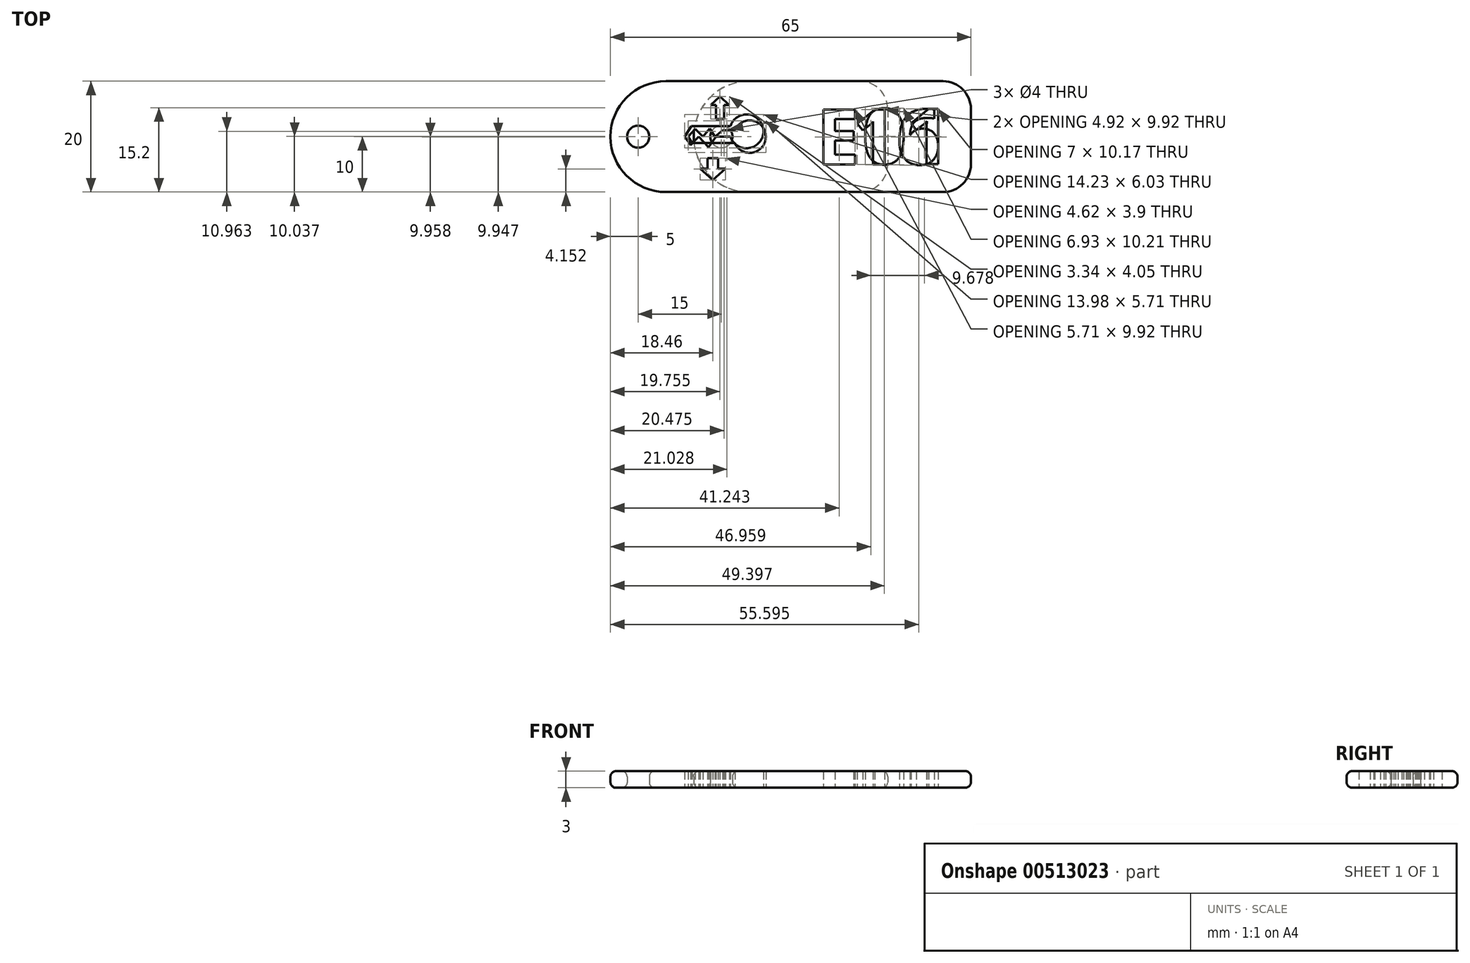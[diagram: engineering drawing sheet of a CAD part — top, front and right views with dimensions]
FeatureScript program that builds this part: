
annotation { "Feature Type Name" : "Feature", "Feature Type Description" : "" }
export const myFeature = defineFeature(function(context is Context, id is Id, definition is map)
    precondition{}
    {
        {
            var Q0;
            Q0=qCreatedBy(makeId("Top.planeOp"),FACE);
            var sketch = newSketch(context, id + "F0", { "sketchPlane" : qUnion([Q0])});
            skLineSegment(sketch, "E0.bottom", {"start": v(27.5, 10) * mm, "end": v(-22.5, 10) * mm});
            skLineSegment(sketch, "E0.top", {"start": v(27.5, -10) * mm, "end": v(-22.5, -10) * mm});
            skLineSegment(sketch, "E0.left", {"start": v(32.5, 5) * mm, "end": v(32.5, -5) * mm});
            skLineSegment(sketch, "E0.right", {"start": v(-32.5, 0) * mm, "end": v(-32.5, 0) * mm});
            skPoint(sketch, "E0.middle", {"position": v(0, 0) * mm});
            skPoint(sketch, "E1.visualSharp", {"position": v(-32.5, 10) * mm});
            skArc(sketch, "E1.filletArc", {"start": v(-22.5, 10) * mm, "mid": v(-29.57, 7.07) * mm, "end": v(-32.5, 0) * mm});
            skPoint(sketch, "E2.visualSharp", {"position": v(-32.5, -10) * mm});
            skArc(sketch, "E2.filletArc", {"start": v(-32.5, 0) * mm, "mid": v(-29.57, -7.07) * mm, "end": v(-22.5, -10) * mm});
            skPoint(sketch, "E3.visualSharp", {"position": v(32.5, 10) * mm});
            skArc(sketch, "E3.filletArc", {"start": v(32.5, 5) * mm, "mid": v(31.04, 8.54) * mm, "end": v(27.5, 10) * mm});
            skPoint(sketch, "E4.visualSharp", {"position": v(32.5, -10) * mm});
            skArc(sketch, "E4.filletArc", {"start": v(27.5, -10) * mm, "mid": v(31.04, -8.54) * mm, "end": v(32.5, -5) * mm});
            skCircle(sketch, "E5", {"center": v(-27.5, 0) * mm, "radius": 2 * mm});
            skText(sketch, "E6", { "text": "01", "fontName": "OpenSans-Bold.ttf"});
            skLineSegment(sketch, "E7", {"start": v(-18.46, 0) * mm, "end": v(-17.2, 1.38) * mm});
            skLineSegment(sketch, "E8", {"start": v(-17.2, 1.38) * mm, "end": v(-15.81, 0) * mm});
            skLineSegment(sketch, "E9", {"start": v(-15.81, 0) * mm, "end": v(-14.64, 1.48) * mm});
            skLineSegment(sketch, "E10", {"start": v(-14.64, 1.48) * mm, "end": v(-13.66, 0) * mm});
            skLineSegment(sketch, "E11", {"start": v(-13.66, 0) * mm, "end": v(-12.27, 1.17) * mm});
            skLineSegment(sketch, "E12", {"start": v(-12.27, 1.17) * mm, "end": v(-10.07, 1.17) * mm});
            skLineSegment(sketch, "E13", {"start": v(-18.46, 0) * mm, "end": v(-17.78, -1.17) * mm});
            skLineSegment(sketch, "E14", {"start": v(-17.78, -1.17) * mm, "end": v(-10.07, -1.17) * mm});
            skArc(sketch, "E15", {"start": v(-10.07, -1.17) * mm, "mid": v(-4.48, 0) * mm, "end": v(-10.07, 1.17) * mm});
            skLineSegment(sketch, "E16", {"start": v(-12.75, 3.17) * mm, "end": v(-13.49, 3.17) * mm});
            skLineSegment(sketch, "E17", {"start": v(-13.49, 3.17) * mm, "end": v(-13.49, 5.7) * mm});
            skLineSegment(sketch, "E18", {"start": v(-13.49, 5.7) * mm, "end": v(-14.42, 5.7) * mm});
            skLineSegment(sketch, "E19", {"start": v(-14.42, 5.7) * mm, "end": v(-12.75, 7.23) * mm});
            skLineSegment(sketch, "E20", {"start": v(-12.75, 7.23) * mm, "end": v(-12.75, 3.17) * mm, "construction": true});
            skLineSegment(sketch, "E21.MirrorCS", {"start": v(-11.07, 5.7) * mm, "end": v(-12.75, 7.23) * mm});
            skLineSegment(sketch, "E22.MirrorCS", {"start": v(-12, 5.7) * mm, "end": v(-11.07, 5.7) * mm});
            skLineSegment(sketch, "E23.MirrorCS", {"start": v(-12, 3.17) * mm, "end": v(-12, 5.7) * mm});
            skLineSegment(sketch, "E24.MirrorCS", {"start": v(-12.75, 3.17) * mm, "end": v(-12, 3.17) * mm});
            skLineSegment(sketch, "E25.MirrorCS", {"start": v(-12.75, -3.17) * mm, "end": v(-12, -3.17) * mm});
            skLineSegment(sketch, "E26.MirrorCS", {"start": v(-13.49, -5.7) * mm, "end": v(-14.42, -5.7) * mm});
            skLineSegment(sketch, "E27.MirrorCS", {"start": v(-12, -3.17) * mm, "end": v(-12, -5.7) * mm});
            skLineSegment(sketch, "E28.MirrorCS", {"start": v(-11.07, -5.7) * mm, "end": v(-12.75, -7.23) * mm});
            skLineSegment(sketch, "E29.MirrorCS", {"start": v(-13.49, -3.17) * mm, "end": v(-13.49, -5.7) * mm});
            skLineSegment(sketch, "E30.MirrorCS", {"start": v(-12, -5.7) * mm, "end": v(-11.07, -5.7) * mm});
            skLineSegment(sketch, "E31.MirrorCS", {"start": v(-14.42, -5.7) * mm, "end": v(-12.75, -7.23) * mm});
            skLineSegment(sketch, "E32.MirrorCS", {"start": v(-12.75, -3.17) * mm, "end": v(-13.49, -3.17) * mm});
            skLineSegment(sketch, "E33.MirrorCS", {"start": v(-12.75, -7.23) * mm, "end": v(-12.75, -3.17) * mm, "construction": true});
            const initialGuessF0  = {"E6": [0.01293, -0.00493, 1, 0, 0.01]};
            skSetInitialGuess(sketch, initialGuessF0);
            skSolve(sketch);
        }
        {
            var Q0;
            Q0=makeQuery(id+"F0.imprint","IMPRINT",FACE,{"disambiguationData":[TD([[makeQuery(id+"F0.imprint","IMPRINT",EDGE,{"derivedFrom":sQuery(id+"F0.wireOp",EDGE,"E0.bottom")}),1.0]])]});
            var Q1;
            Q1=makeQuery(id+"F0.imprint","IMPRINT",FACE,{"disambiguationData":[TD([[makeQuery(id+"F0.imprint","IMPRINT",EDGE,{"derivedFrom":sQuery(id+"F0.wireOp",EDGE,"E28.MirrorCS")}),-1.0]])]});
            extrude(context, id + "F1", {"entities" : qUnion([Q0, Q1]), "depth" : 3 * mm});
        }
        {
            var Q0;
            Q0=makeQuery(id+"F1.opExtrude","CAP_EDGE",EDGE,{"disambiguationData":[OSD([sQuery(id+"F0.wireOp",EDGE,"E0.top")])],"isStart":false});
            var Q1;
            Q1=makeQuery(id+"F1.opExtrude","CAP_EDGE",EDGE,{"disambiguationData":[OSD([sQuery(id+"F0.wireOp",EDGE,"E0.top")])],"isStart":true});
            var Q2;
            Q2=makeQuery(id+"F1.opExtrude","CAP_EDGE",EDGE,{"disambiguationData":[OSD([sQuery(id+"F0.wireOp",EDGE,"E5")])],"isStart":false});
            var Q3;
            Q3=makeQuery(id+"F1.opExtrude","CAP_EDGE",EDGE,{"disambiguationData":[OSD([sQuery(id+"F0.wireOp",EDGE,"E5")])],"isStart":true});
            fillet(context, id + "F2", {"entities" : qUnion([Q0, Q1, Q2, Q3]), "radius" : 1 * mm, "tangentPropagation" : true, "allowEdgeOverflow" : false});
        }
        {
            var Q0;
            Q0=qCreatedBy(makeId("Top.planeOp"),FACE);
            var sketch = newSketch(context, id + "F3", { "sketchPlane" : qUnion([Q0])});
            skLineSegment(sketch, "E34.bottom", {"start": v(27.5, 10) * mm, "end": v(-22.5, 10) * mm});
            skLineSegment(sketch, "E34.top", {"start": v(27.5, -10) * mm, "end": v(-22.5, -10) * mm});
            skLineSegment(sketch, "E34.left", {"start": v(32.5, 5) * mm, "end": v(32.5, -5) * mm});
            skLineSegment(sketch, "E34.right", {"start": v(-32.5, 0) * mm, "end": v(-32.5, 0) * mm});
            skPoint(sketch, "E34.middle", {"position": v(0, 0) * mm});
            skPoint(sketch, "E35.visualSharp", {"position": v(-32.5, 10) * mm});
            skArc(sketch, "E35.filletArc", {"start": v(-22.5, 10) * mm, "mid": v(-29.57, 7.07) * mm, "end": v(-32.5, 0) * mm});
            skPoint(sketch, "E36.visualSharp", {"position": v(-32.5, -10) * mm});
            skArc(sketch, "E36.filletArc", {"start": v(-32.5, 0) * mm, "mid": v(-29.57, -7.07) * mm, "end": v(-22.5, -10) * mm});
            skPoint(sketch, "E37.visualSharp", {"position": v(32.5, 10) * mm});
            skArc(sketch, "E37.filletArc", {"start": v(32.5, 5) * mm, "mid": v(31.04, 8.54) * mm, "end": v(27.5, 10) * mm});
            skPoint(sketch, "E38.visualSharp", {"position": v(32.5, -10) * mm});
            skArc(sketch, "E38.filletArc", {"start": v(27.5, -10) * mm, "mid": v(31.04, -8.54) * mm, "end": v(32.5, -5) * mm});
            skCircle(sketch, "E39", {"center": v(-27.5, 0) * mm, "radius": 2 * mm});
            skText(sketch, "E40", { "text": "16", "fontName": "OpenSans-Bold.ttf"});
            skLineSegment(sketch, "E41", {"start": v(-19.14, 0) * mm, "end": v(-18.04, -1.51) * mm});
            skLineSegment(sketch, "E42", {"start": v(-18.04, -1.51) * mm, "end": v(-16.58, 0) * mm});
            skLineSegment(sketch, "E43", {"start": v(-16.58, 0) * mm, "end": v(-14.78, -1.9) * mm});
            skLineSegment(sketch, "E44", {"start": v(-14.78, -1.9) * mm, "end": v(-13.44, 0) * mm});
            skLineSegment(sketch, "E45", {"start": v(-13.44, 0) * mm, "end": v(-10.87, 0) * mm});
            skLineSegment(sketch, "E46", {"start": v(-19.14, 0) * mm, "end": v(-17.91, 1.93) * mm});
            skLineSegment(sketch, "E47", {"start": v(-17.91, 1.93) * mm, "end": v(-10.87, 1.93) * mm});
            skArc(sketch, "E48", {"start": v(-10.87, 0) * mm, "mid": v(-4.9, 0.96) * mm, "end": v(-10.87, 1.93) * mm});
            skLineSegment(sketch, "E49", {"start": v(-14.98, -3.9) * mm, "end": v(-14.98, -5.78) * mm});
            skLineSegment(sketch, "E50", {"start": v(-14.98, -5.78) * mm, "end": v(-16.35, -5.78) * mm});
            skLineSegment(sketch, "E51", {"start": v(-16.35, -5.78) * mm, "end": v(-14.04, -7.8) * mm});
            skLineSegment(sketch, "E52", {"start": v(-14.98, -3.9) * mm, "end": v(-14.04, -3.9) * mm});
            skLineSegment(sketch, "E53", {"start": v(-14.04, -3.9) * mm, "end": v(-14.04, -7.8) * mm, "construction": true});
            skLineSegment(sketch, "E54.MirrorCS", {"start": v(-13.1, -3.9) * mm, "end": v(-14.04, -3.9) * mm});
            skLineSegment(sketch, "E55.MirrorCS", {"start": v(-13.1, -3.9) * mm, "end": v(-13.1, -5.78) * mm});
            skLineSegment(sketch, "E56.MirrorCS", {"start": v(-13.1, -5.78) * mm, "end": v(-11.73, -5.78) * mm});
            skLineSegment(sketch, "E57.MirrorCS", {"start": v(-11.73, -5.78) * mm, "end": v(-14.04, -7.8) * mm});
            const initialGuessF3  = {"E40": [0.01118, -0.005, 1, 0, 0.01]};
            skSetInitialGuess(sketch, initialGuessF3);
            skSolve(sketch);
        }
        {
            var Q0;
            Q0 = qSketchRegion(id + "F3", true);
            extrude(context, id + "F4", {"entities" : qUnion([Q0]), "depth" : 3 * mm});
        }
        {
            var Q0;
            Q0=makeQuery(id+"F4.opExtrude","CAP_EDGE",EDGE,{"disambiguationData":[OSD([sQuery(id+"F3.wireOp",EDGE,"E34.top")])],"isStart":false});
            var Q1;
            Q1=makeQuery(id+"F4.opExtrude","CAP_EDGE",EDGE,{"disambiguationData":[OSD([sQuery(id+"F3.wireOp",EDGE,"E34.top")])],"isStart":true});
            var Q2;
            Q2=makeQuery(id+"F4.opExtrude","CAP_EDGE",EDGE,{"disambiguationData":[OSD([sQuery(id+"F3.wireOp",EDGE,"E39")])],"isStart":false});
            var Q3;
            Q3=makeQuery(id+"F4.opExtrude","CAP_EDGE",EDGE,{"disambiguationData":[OSD([sQuery(id+"F3.wireOp",EDGE,"E39")])],"isStart":true});
            fillet(context, id + "F5", {"entities" : qUnion([Q0, Q1, Q2, Q3]), "radius" : 1 * mm, "tangentPropagation" : true, "allowEdgeOverflow" : false});
        }
        {
            var Q0;
            Q0=qCreatedBy(makeId("Top.planeOp"),FACE);
            var sketch = newSketch(context, id + "F6", { "sketchPlane" : qUnion([Q0])});
            skLineSegment(sketch, "E58.bottom", {"start": v(12.5, 10) * mm, "end": v(-7.5, 10) * mm});
            skLineSegment(sketch, "E58.top", {"start": v(12.5, -10) * mm, "end": v(-7.5, -10) * mm});
            skLineSegment(sketch, "E58.left", {"start": v(17.5, 5) * mm, "end": v(17.5, -5) * mm});
            skLineSegment(sketch, "E58.right", {"start": v(-17.5, 0) * mm, "end": v(-17.5, 0) * mm});
            skPoint(sketch, "E58.middle", {"position": v(0, 0) * mm});
            skPoint(sketch, "E59.visualSharp", {"position": v(-17.5, 10) * mm});
            skArc(sketch, "E59.filletArc", {"start": v(-7.5, 10) * mm, "mid": v(-14.57, 7.07) * mm, "end": v(-17.5, 0) * mm});
            skPoint(sketch, "E60.visualSharp", {"position": v(-17.5, -10) * mm});
            skArc(sketch, "E60.filletArc", {"start": v(-17.5, 0) * mm, "mid": v(-14.57, -7.07) * mm, "end": v(-7.5, -10) * mm});
            skPoint(sketch, "E61.visualSharp", {"position": v(17.5, 10) * mm});
            skArc(sketch, "E61.filletArc", {"start": v(17.5, 5) * mm, "mid": v(16.04, 8.54) * mm, "end": v(12.5, 10) * mm});
            skPoint(sketch, "E62.visualSharp", {"position": v(17.5, -10) * mm});
            skArc(sketch, "E62.filletArc", {"start": v(12.5, -10) * mm, "mid": v(16.04, -8.54) * mm, "end": v(17.5, -5) * mm});
            skCircle(sketch, "E63", {"center": v(-12.5, 0) * mm, "radius": 2 * mm});
            skText(sketch, "E64", { "text": "E", "fontName": "OpenSans-Bold.ttf"});
            const initialGuessF6  = {"E64": [0.00464, -0.005, 1, 0, 0.01]};
            skSetInitialGuess(sketch, initialGuessF6);
            skSolve(sketch);
        }
        {
            var Q0;
            Q0=makeQuery(id+"F6.imprint","IMPRINT",FACE,{"disambiguationData":[TD([[makeQuery(id+"F6.imprint","IMPRINT",EDGE,{"derivedFrom":sQuery(id+"F6.wireOp",EDGE,"E58.bottom")}),1.0]])]});
            extrude(context, id + "F7", {"entities" : qUnion([Q0]), "depth" : 3 * mm, "offsetDistance" : 25 * mm});
        }
        {
            var Q0;
            Q0=makeQuery(id+"F7.opExtrude","CAP_EDGE",EDGE,{"disambiguationData":[OSD([sQuery(id+"F6.wireOp",EDGE,"E58.top")])],"isStart":false});
            var Q1;
            Q1=makeQuery(id+"F7.opExtrude","CAP_EDGE",EDGE,{"disambiguationData":[OSD([sQuery(id+"F6.wireOp",EDGE,"E58.top")])],"isStart":true});
            var Q2;
            Q2=makeQuery(id+"F7.opExtrude","CAP_EDGE",EDGE,{"disambiguationData":[OSD([sQuery(id+"F6.wireOp",EDGE,"E63")])],"isStart":false});
            var Q3;
            Q3=makeQuery(id+"F7.opExtrude","SWEPT_FACE",FACE,{"disambiguationData":[OSD([sQuery(id+"F6.wireOp",EDGE,"E63")])]});
            fillet(context, id + "F8", {"entities" : qUnion([Q0, Q1, Q2, Q3]), "radius" : 1 * mm, "tangentPropagation" : true, "allowEdgeOverflow" : false});
        }
    });
